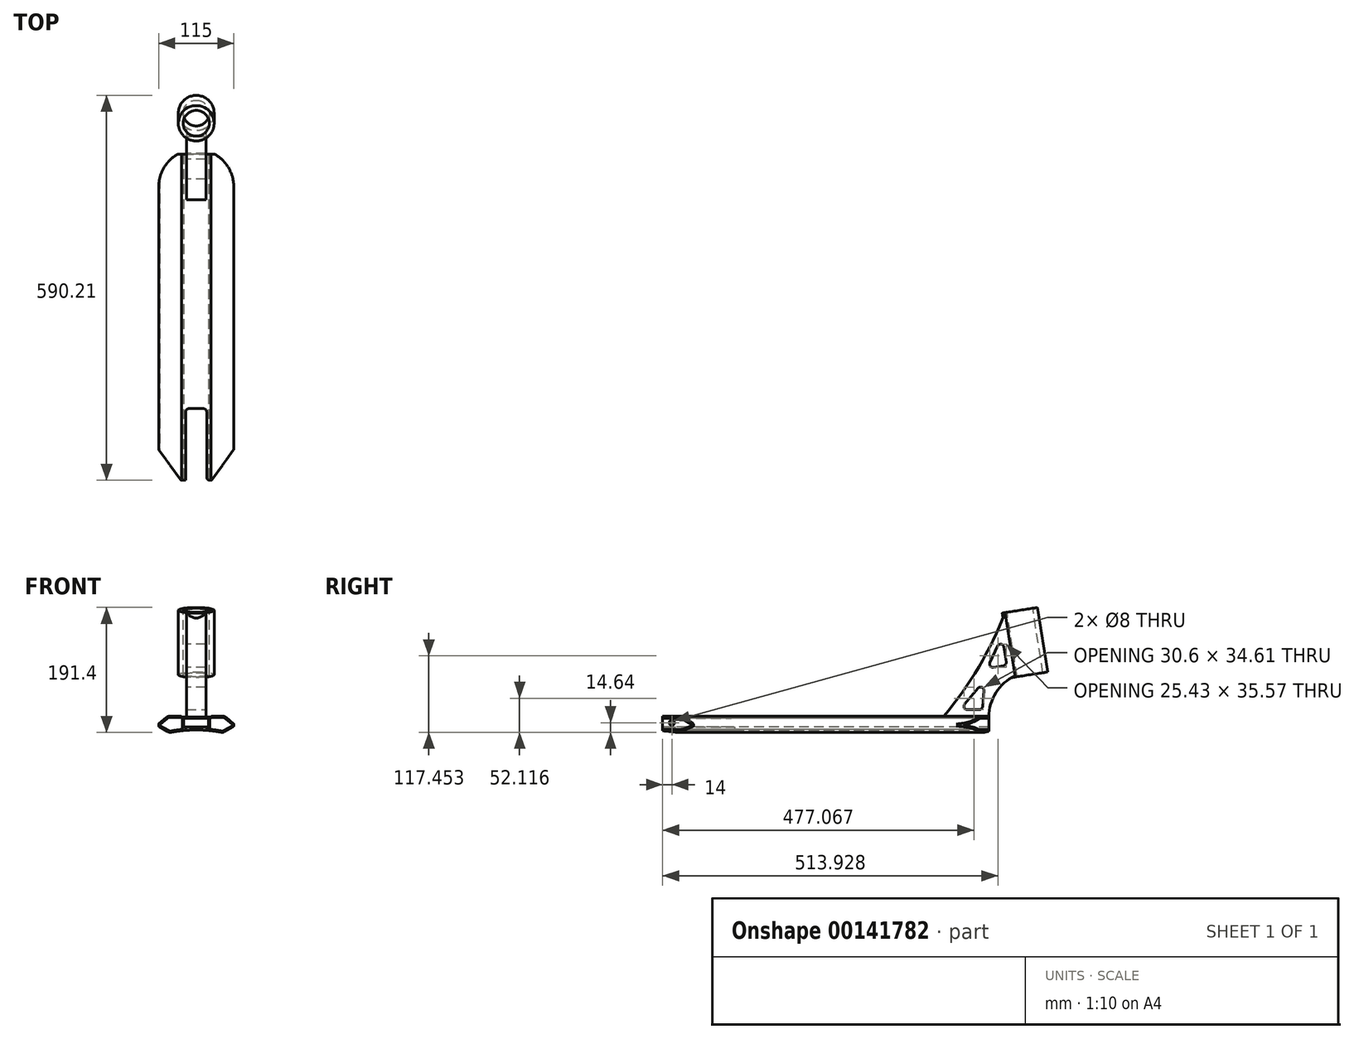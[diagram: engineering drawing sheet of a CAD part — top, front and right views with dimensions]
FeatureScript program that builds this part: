
annotation { "Feature Type Name" : "Feature", "Feature Type Description" : "" }
export const myFeature = defineFeature(function(context is Context, id is Id, definition is map)
    precondition{}
    {
        {
            var Q0;
            Q0=qCreatedBy(makeId("Front.planeOp"),FACE);
            var sketch = newSketch(context, id + "F0", { "sketchPlane" : qUnion([Q0])});
            skLineSegment(sketch, "E0", {"start": v(0, 0) * mm, "end": v(0, 43.35) * mm, "construction": true});
            skLineSegment(sketch, "E1", {"start": v(0, 25.68) * mm, "end": v(22.5, 25.68) * mm});
            skLineSegment(sketch, "E2", {"start": v(22.5, 25.68) * mm, "end": v(22.5, 26.98) * mm});
            skLineSegment(sketch, "E3", {"start": v(22.5, 26.98) * mm, "end": v(43.54, 26.98) * mm});
            skLineSegment(sketch, "E4", {"start": v(43.54, 26.98) * mm, "end": v(57.5, 15.27) * mm});
            skLineSegment(sketch, "E5", {"start": v(57.5, 15.27) * mm, "end": v(57.5, 11.27) * mm});
            skLineSegment(sketch, "E6", {"start": v(57.5, 11.27) * mm, "end": v(40.89, 1.68) * mm});
            skLineSegment(sketch, "E7.MirrorCS", {"start": v(-22.5, 26.98) * mm, "end": v(-43.54, 26.98) * mm});
            skLineSegment(sketch, "E8.MirrorCS", {"start": v(-22.5, 25.68) * mm, "end": v(-22.5, 26.98) * mm});
            skLineSegment(sketch, "E9.MirrorCS", {"start": v(-43.54, 26.98) * mm, "end": v(-57.5, 15.27) * mm});
            skLineSegment(sketch, "E10.MirrorCS", {"start": v(-57.5, 11.27) * mm, "end": v(-40.89, 1.68) * mm});
            skLineSegment(sketch, "E11.MirrorCS", {"start": v(0, 25.68) * mm, "end": v(-22.5, 25.68) * mm});
            skLineSegment(sketch, "E12.MirrorCS", {"start": v(-57.5, 15.27) * mm, "end": v(-57.5, 11.27) * mm});
            skArc(sketch, "E13", {"start": v(40.89, 1.68) * mm, "mid": v(0, 5.9) * mm, "end": v(-40.89, 1.68) * mm});
            skSolve(sketch);
        }
        {
            var Q0;
            Q0 = qSketchRegion(id + "F0", true);
            extrude(context, id + "F1", {"entities" : qUnion([Q0]), "endBound" : BoundingType.SYMMETRIC, "depth" : 500 * mm});
        }
        {
            var Q0;
            Q0=qCreatedBy(makeId("Front.planeOp"),FACE);
            var sketch = newSketch(context, id + "F2", { "sketchPlane" : qUnion([Q0])});
            skLineSegment(sketch, "E14.bottom", {"start": v(-19, 23.68) * mm, "end": v(19, 23.68) * mm});
            skLineSegment(sketch, "E14.top", {"start": v(-19, 10.68) * mm, "end": v(19, 10.68) * mm});
            skLineSegment(sketch, "E14.left", {"start": v(-19, 23.68) * mm, "end": v(-19, 10.68) * mm});
            skLineSegment(sketch, "E14.right", {"start": v(19, 23.68) * mm, "end": v(19, 10.68) * mm});
            skSolve(sketch);
        }
        {
            var Q0;
            Q0 = qSketchRegion(id + "F2", true);
            extrude(context, id + "F3", {"entities" : qUnion([Q0]), "operationType" : NewBodyOperationType.REMOVE, "endBound" : BoundingType.SYMMETRIC, "oppositeDirection" : true, "depth" : 500 * mm});
        }
        {
            var Q0;
            Q0=makeQuery(id+"F1.opExtrude","SWEPT_EDGE",EDGE,{"disambiguationData":[OSD([sQuery(id+"F0.wireOp",EDGE,"E7.MirrorCS"),sQuery(id+"F0.wireOp",EDGE,"E8.MirrorCS")])]});
            var Q1;
            Q1=makeQuery(id+"F1.opExtrude","SWEPT_EDGE",EDGE,{"disambiguationData":[OSD([sQuery(id+"F0.wireOp",EDGE,"E2"),sQuery(id+"F0.wireOp",EDGE,"E3")])]});
            fillet(context, id + "F4", {"entities" : qUnion([Q0, Q1]), "radius" : 2 * mm, "tangentPropagation" : true, "allowEdgeOverflow" : false});
        }
        {
            var Q0;
            Q0=makeQuery(id+"F1.opExtrude","SWEPT_EDGE",EDGE,{"disambiguationData":[OSD([sQuery(id+"F0.wireOp",EDGE,"E3"),sQuery(id+"F0.wireOp",EDGE,"E4")])]});
            var Q1;
            Q1=makeQuery(id+"F1.opExtrude","SWEPT_EDGE",EDGE,{"disambiguationData":[OSD([sQuery(id+"F0.wireOp",EDGE,"E7.MirrorCS"),sQuery(id+"F0.wireOp",EDGE,"E9.MirrorCS")])]});
            var Q2;
            Q2=makeQuery(id+"F1.opExtrude","SWEPT_EDGE",EDGE,{"disambiguationData":[OSD([sQuery(id+"F0.wireOp",EDGE,"E10.MirrorCS"),sQuery(id+"F0.wireOp",EDGE,"E13")])]});
            var Q3;
            Q3=makeQuery(id+"F1.opExtrude","SWEPT_EDGE",EDGE,{"disambiguationData":[OSD([sQuery(id+"F0.wireOp",EDGE,"E6"),sQuery(id+"F0.wireOp",EDGE,"E13")])]});
            fillet(context, id + "F5", {"entities" : qUnion([Q0, Q1, Q2, Q3]), "radius" : 9 * mm, "tangentPropagation" : true, "allowEdgeOverflow" : false});
        }
        {
            var Q0;
            Q0=makeQuery(id+"F1.opExtrude","SWEPT_EDGE",EDGE,{"disambiguationData":[OSD([sQuery(id+"F0.wireOp",EDGE,"E4"),sQuery(id+"F0.wireOp",EDGE,"E5")])]});
            var Q1;
            Q1=makeQuery(id+"F1.opExtrude","SWEPT_EDGE",EDGE,{"disambiguationData":[OSD([sQuery(id+"F0.wireOp",EDGE,"E5"),sQuery(id+"F0.wireOp",EDGE,"E6")])]});
            var Q2;
            Q2=makeQuery(id+"F1.opExtrude","SWEPT_EDGE",EDGE,{"disambiguationData":[OSD([sQuery(id+"F0.wireOp",EDGE,"E9.MirrorCS"),sQuery(id+"F0.wireOp",EDGE,"E12.MirrorCS")])]});
            var Q3;
            Q3=makeQuery(id+"F1.opExtrude","SWEPT_EDGE",EDGE,{"disambiguationData":[OSD([sQuery(id+"F0.wireOp",EDGE,"E10.MirrorCS"),sQuery(id+"F0.wireOp",EDGE,"E12.MirrorCS")])]});
            fillet(context, id + "F6", {"entities" : qUnion([Q0, Q1, Q2, Q3]), "radius" : 1 * mm, "tangentPropagation" : true, "allowEdgeOverflow" : false});
        }
        {
            var Q0;
            Q0=makeQuery(id+"F1.opExtrude","CAP_FACE",FACE,{"disambiguationData":[OSD([sQuery(id+"F0.wireOp",EDGE,"E1"),sQuery(id+"F0.wireOp",EDGE,"E2"),sQuery(id+"F0.wireOp",EDGE,"E3"),sQuery(id+"F0.wireOp",EDGE,"E4"),sQuery(id+"F0.wireOp",EDGE,"E5"),sQuery(id+"F0.wireOp",EDGE,"E6"),sQuery(id+"F0.wireOp",EDGE,"E7.MirrorCS"),sQuery(id+"F0.wireOp",EDGE,"E8.MirrorCS"),sQuery(id+"F0.wireOp",EDGE,"E9.MirrorCS"),sQuery(id+"F0.wireOp",EDGE,"E10.MirrorCS"),sQuery(id+"F0.wireOp",EDGE,"E11.MirrorCS"),sQuery(id+"F0.wireOp",EDGE,"E12.MirrorCS"),sQuery(id+"F0.wireOp",EDGE,"E13")])],"isStart":false});
            var sketch = newSketch(context, id + "F7", { "sketchPlane" : qUnion([Q0])});
            skLineSegment(sketch, "E15.0.0", {"start": v(-46.05, 24.87) * mm, "end": v(-57.14, 15.57) * mm});
            skArc(sketch, "E15.0.1", {"start": v(-57.14, 15.57) * mm, "mid": v(-57.4, 15.23) * mm, "end": v(-57.5, 14.8) * mm});
            skLineSegment(sketch, "E15.0.2", {"start": v(-57.5, 14.8) * mm, "end": v(-57.5, 11.85) * mm});
            skArc(sketch, "E15.0.3", {"start": v(-57.5, 11.85) * mm, "mid": v(-57.37, 11.35) * mm, "end": v(-57, 10.98) * mm});
            skLineSegment(sketch, "E15.0.4", {"start": v(-57, 10.98) * mm, "end": v(-43.83, 3.38) * mm});
            skArc(sketch, "E15.0.5", {"start": v(-43.83, 3.38) * mm, "mid": v(-40.83, 2.3) * mm, "end": v(-37.64, 2.33) * mm});
            skArc(sketch, "E15.0.6", {"start": v(-37.64, 2.33) * mm, "mid": v(0, 5.9) * mm, "end": v(37.64, 2.33) * mm});
            skArc(sketch, "E15.0.7", {"start": v(37.64, 2.33) * mm, "mid": v(40.83, 2.3) * mm, "end": v(43.83, 3.38) * mm});
            skLineSegment(sketch, "E15.0.8", {"start": v(43.83, 3.38) * mm, "end": v(57, 10.98) * mm});
            skArc(sketch, "E15.0.9", {"start": v(57, 10.98) * mm, "mid": v(57.37, 11.35) * mm, "end": v(57.5, 11.85) * mm});
            skLineSegment(sketch, "E15.0.10", {"start": v(57.5, 11.85) * mm, "end": v(57.5, 14.8) * mm});
            skArc(sketch, "E15.0.11", {"start": v(57.5, 14.8) * mm, "mid": v(57.4, 15.23) * mm, "end": v(57.14, 15.57) * mm});
            skLineSegment(sketch, "E15.0.12", {"start": v(57.14, 15.57) * mm, "end": v(46.05, 24.87) * mm});
            skArc(sketch, "E15.0.13", {"start": v(46.05, 24.87) * mm, "mid": v(43.35, 26.44) * mm, "end": v(40.27, 26.98) * mm});
            skLineSegment(sketch, "E15.0.14", {"start": v(40.27, 26.98) * mm, "end": v(24.37, 26.98) * mm});
            skArc(sketch, "E15.0.15", {"start": v(24.37, 26.98) * mm, "mid": v(23.23, 26.62) * mm, "end": v(22.5, 25.68) * mm});
            skLineSegment(sketch, "E15.0.16", {"start": v(22.5, 25.68) * mm, "end": v(-22.5, 25.68) * mm});
            skArc(sketch, "E15.0.17", {"start": v(-22.5, 25.68) * mm, "mid": v(-23.23, 26.62) * mm, "end": v(-24.37, 26.98) * mm});
            skLineSegment(sketch, "E15.0.18", {"start": v(-24.37, 26.98) * mm, "end": v(-40.27, 26.98) * mm});
            skArc(sketch, "E15.0.19", {"start": v(-40.27, 26.98) * mm, "mid": v(-43.35, 26.44) * mm, "end": v(-46.05, 24.87) * mm});
            skLineSegment(sketch, "E16.0", {"start": v(40.27, 24.98) * mm, "end": v(24.37, 24.98) * mm});
            skLineSegment(sketch, "E16.1", {"start": v(-55.61, 12.5) * mm, "end": v(-42.83, 5.1) * mm});
            skLineSegment(sketch, "E16.2", {"start": v(-44.77, 23.34) * mm, "end": v(-55.76, 14.12) * mm});
            skArc(sketch, "E16.3", {"start": v(-40.27, 24.98) * mm, "mid": v(-42.66, 24.56) * mm, "end": v(-44.77, 23.34) * mm});
            skLineSegment(sketch, "E16.4", {"start": v(-24.37, 24.98) * mm, "end": v(-40.27, 24.98) * mm});
            skArc(sketch, "E16.5", {"start": v(-42.83, 5.1) * mm, "mid": v(-40.5, 4.27) * mm, "end": v(-38.01, 4.3) * mm});
            skArc(sketch, "E16.6", {"start": v(-38.01, 4.3) * mm, "mid": v(-29.53, 5.73) * mm, "end": v(-21, 6.81) * mm});
            skArc(sketch, "E16.7", {"start": v(38.01, 4.3) * mm, "mid": v(40.5, 4.27) * mm, "end": v(42.83, 5.1) * mm});
            skLineSegment(sketch, "E16.8", {"start": v(42.83, 5.1) * mm, "end": v(55.61, 12.5) * mm});
            skLineSegment(sketch, "E16.9", {"start": v(55.76, 14.12) * mm, "end": v(44.77, 23.34) * mm});
            skArc(sketch, "E16.10", {"start": v(44.77, 23.34) * mm, "mid": v(42.66, 24.56) * mm, "end": v(40.27, 24.98) * mm});
            skLineSegment(sketch, "E17", {"start": v(-21, 23.68) * mm, "end": v(-21, 6.81) * mm});
            skLineSegment(sketch, "E18", {"start": v(-22.5, 23.68) * mm, "end": v(-21, 23.68) * mm});
            skArc(sketch, "E19", {"start": v(-22.5, 23.68) * mm, "mid": v(-23.23, 24.62) * mm, "end": v(-24.37, 24.98) * mm});
            skLineSegment(sketch, "E20", {"start": v(21, 23.68) * mm, "end": v(21, 6.81) * mm});
            skLineSegment(sketch, "E21", {"start": v(21, 23.68) * mm, "end": v(22.5, 23.68) * mm});
            skArc(sketch, "E22", {"start": v(24.37, 24.98) * mm, "mid": v(23.23, 24.62) * mm, "end": v(22.5, 23.68) * mm});
            skArc(sketch, "E23.trimOffspring", {"start": v(21, 6.81) * mm, "mid": v(29.53, 5.73) * mm, "end": v(38.01, 4.3) * mm});
            skPoint(sketch, "E24.visualSharp", {"position": v(-56.85, 13.2) * mm});
            skArc(sketch, "E24.filletArc", {"start": v(-55.76, 14.12) * mm, "mid": v(-56.1, 13.27) * mm, "end": v(-55.61, 12.5) * mm});
            skPoint(sketch, "E25.visualSharp", {"position": v(56.85, 13.2) * mm});
            skArc(sketch, "E25.filletArc", {"start": v(55.61, 12.5) * mm, "mid": v(56.1, 13.27) * mm, "end": v(55.76, 14.12) * mm});
            skSolve(sketch);
        }
        {
            var Q0;
            Q0=makeQuery(id+"F7.imprint","IMPRINT",FACE,{"disambiguationData":[TD([[makeQuery(id+"F7.imprint","IMPRINT",EDGE,{"derivedFrom":sQuery(id+"F7.wireOp",EDGE,"E16.1")}),1.0]])]});
            var Q1;
            Q1=makeQuery(id+"F7.imprint","IMPRINT",FACE,{"disambiguationData":[TD([[makeQuery(id+"F7.imprint","IMPRINT",EDGE,{"derivedFrom":sQuery(id+"F7.wireOp",EDGE,"E16.0")}),1.0]])]});
            extrude(context, id + "F8", {"entities" : qUnion([Q0, Q1]), "operationType" : NewBodyOperationType.REMOVE, "endBound" : BoundingType.THROUGH_ALL, "oppositeDirection" : true, "depth" : 25 * mm});
        }
        {
            var Q0;
            Q0=qCreatedBy(makeId("Top.planeOp"),FACE);
            var sketch = newSketch(context, id + "F9", { "sketchPlane" : qUnion([Q0])});
            skArc(sketch, "E26", {"start": v(57.5, 200) * mm, "mid": v(0, 257.5) * mm, "end": v(-57.5, 200) * mm});
            skLineSegment(sketch, "E27", {"start": v(-57.5, 200) * mm, "end": v(-57.5, 280) * mm});
            skLineSegment(sketch, "E28", {"start": v(57.5, 200) * mm, "end": v(57.5, 280) * mm});
            skLineSegment(sketch, "E29", {"start": v(57.5, 280) * mm, "end": v(-57.5, 280) * mm});
            skSolve(sketch);
        }
        {
            var Q0;
            Q0 = qSketchRegion(id + "F9", true);
            extrude(context, id + "F10", {"entities" : qUnion([Q0]), "operationType" : NewBodyOperationType.REMOVE, "endBound" : BoundingType.THROUGH_ALL, "depth" : 25 * mm});
        }
        {
            var Q0;
            Q0=qCreatedBy(makeId("Top.planeOp"),FACE);
            var sketch = newSketch(context, id + "F11", { "sketchPlane" : qUnion([Q0])});
            skLineSegment(sketch, "E30", {"start": v(-57.5, -203) * mm, "end": v(-57.5, -303) * mm});
            skLineSegment(sketch, "E31", {"start": v(-57.5, -303) * mm, "end": v(57.5, -303) * mm});
            skLineSegment(sketch, "E32", {"start": v(57.5, -303) * mm, "end": v(57.5, -203) * mm});
            skLineSegment(sketch, "E33", {"start": v(57.5, -203) * mm, "end": v(23.35, -250) * mm});
            skLineSegment(sketch, "E34", {"start": v(23.35, -250) * mm, "end": v(16, -250) * mm});
            skLineSegment(sketch, "E35", {"start": v(16, -250) * mm, "end": v(16, -140) * mm});
            skLineSegment(sketch, "E36", {"start": v(16, -140) * mm, "end": v(-16, -140) * mm});
            skLineSegment(sketch, "E37", {"start": v(-16, -140) * mm, "end": v(-16, -250) * mm});
            skLineSegment(sketch, "E38", {"start": v(-16, -250) * mm, "end": v(-23.35, -250) * mm});
            skLineSegment(sketch, "E39", {"start": v(-23.35, -250) * mm, "end": v(-57.5, -203) * mm});
            skLineSegment(sketch, "E40.bottom", {"start": v(57.5, -203) * mm, "end": v(68, -203) * mm});
            skLineSegment(sketch, "E40.top", {"start": v(57.5, -257) * mm, "end": v(68, -257) * mm});
            skLineSegment(sketch, "E40.left", {"start": v(57.5, -203) * mm, "end": v(57.5, -257) * mm});
            skLineSegment(sketch, "E40.right", {"start": v(68, -203) * mm, "end": v(68, -257) * mm});
            skLineSegment(sketch, "E41.bottom", {"start": v(-57.5, -203) * mm, "end": v(-68, -203) * mm});
            skLineSegment(sketch, "E41.top", {"start": v(-57.5, -257) * mm, "end": v(-68, -257) * mm});
            skLineSegment(sketch, "E41.left", {"start": v(-57.5, -203) * mm, "end": v(-57.5, -257) * mm});
            skLineSegment(sketch, "E41.right", {"start": v(-68, -203) * mm, "end": v(-68, -257) * mm});
            skSolve(sketch);
        }
        {
            var Q0;
            Q0 = qSketchRegion(id + "F11", true);
            extrude(context, id + "F12", {"entities" : qUnion([Q0]), "operationType" : NewBodyOperationType.REMOVE, "endBound" : BoundingType.THROUGH_ALL, "depth" : 25 * mm});
        }
        {
            var Q0;
            {var subQ2=sQuery(id+"F11.wireOp",EDGE,"E37");Q0=makeQuery(id+"F12.boolean.opBoolean","COPY",EDGE,{"disambiguationData":[TD([makeQuery(id+"F3.boolean.opBoolean","COPY",FACE,{"derivedFrom":makeQuery(id+"F3.opExtrude","SWEPT_FACE",FACE,{"disambiguationData":[OSD([sQuery(id+"F2.wireOp",EDGE,"E14.bottom")])]})})])],"derivedFrom":makeQuery(id+"F12.opExtrude","SWEPT_EDGE",EDGE,{"disambiguationData":[OSD([subQ2,sQuery(id+"F11.wireOp",EDGE,"E38")])]})});}
            var Q1;
            {var subQ0=sQuery(id+"F11.wireOp",EDGE,"E36");var subQ1=sQuery(id+"F11.wireOp",EDGE,"E37");Q1=makeQuery(id+"F12.boolean.opBoolean","COPY",EDGE,{"disambiguationData":[TD([makeQuery(id+"F3.boolean.opBoolean","COPY",FACE,{"derivedFrom":makeQuery(id+"F3.opExtrude","SWEPT_FACE",FACE,{"disambiguationData":[OSD([sQuery(id+"F2.wireOp",EDGE,"E14.bottom")])]})})])],"derivedFrom":makeQuery(id+"F12.opExtrude","SWEPT_EDGE",EDGE,{"disambiguationData":[OSD([subQ0,subQ1])]})});}
            var Q2;
            {var subQ0=sQuery(id+"F11.wireOp",EDGE,"E36");var subQ1=sQuery(id+"F11.wireOp",EDGE,"E37");Q2=makeQuery(id+"F12.boolean.opBoolean","COPY",EDGE,{"disambiguationData":[TD([makeQuery(id+"F1.opExtrude","SWEPT_FACE",FACE,{"disambiguationData":[OSD([sQuery(id+"F0.wireOp",EDGE,"E13")])]})])],"derivedFrom":makeQuery(id+"F12.opExtrude","SWEPT_EDGE",EDGE,{"disambiguationData":[OSD([subQ0,subQ1])]})});}
            var Q3;
            {var subQ2=sQuery(id+"F11.wireOp",EDGE,"E35");Q3=makeQuery(id+"F12.boolean.opBoolean","COPY",EDGE,{"disambiguationData":[TD([makeQuery(id+"F3.boolean.opBoolean","COPY",FACE,{"derivedFrom":makeQuery(id+"F3.opExtrude","SWEPT_FACE",FACE,{"disambiguationData":[OSD([sQuery(id+"F2.wireOp",EDGE,"E14.bottom")])]})})])],"derivedFrom":makeQuery(id+"F12.opExtrude","SWEPT_EDGE",EDGE,{"disambiguationData":[OSD([sQuery(id+"F11.wireOp",EDGE,"E34"),subQ2])]})});}
            var Q4;
            {var subQ0=sQuery(id+"F11.wireOp",EDGE,"E35");var subQ1=sQuery(id+"F11.wireOp",EDGE,"E36");Q4=makeQuery(id+"F12.boolean.opBoolean","COPY",EDGE,{"disambiguationData":[TD([makeQuery(id+"F1.opExtrude","SWEPT_FACE",FACE,{"disambiguationData":[OSD([sQuery(id+"F0.wireOp",EDGE,"E13")])]})])],"derivedFrom":makeQuery(id+"F12.opExtrude","SWEPT_EDGE",EDGE,{"disambiguationData":[OSD([subQ0,subQ1])]})});}
            var Q5;
            {var subQ0=sQuery(id+"F11.wireOp",EDGE,"E35");var subQ1=sQuery(id+"F11.wireOp",EDGE,"E36");Q5=makeQuery(id+"F12.boolean.opBoolean","COPY",EDGE,{"disambiguationData":[TD([makeQuery(id+"F3.boolean.opBoolean","COPY",FACE,{"derivedFrom":makeQuery(id+"F3.opExtrude","SWEPT_FACE",FACE,{"disambiguationData":[OSD([sQuery(id+"F2.wireOp",EDGE,"E14.bottom")])]})})])],"derivedFrom":makeQuery(id+"F12.opExtrude","SWEPT_EDGE",EDGE,{"disambiguationData":[OSD([subQ0,subQ1])]})});}
            fillet(context, id + "F13", {"entities" : qUnion([Q0, Q1, Q2, Q3, Q4, Q5]), "radius" : 5 * mm, "tangentPropagation" : true, "allowEdgeOverflow" : false});
        }
        {
            var Q0;
            Q0=qCreatedBy(makeId("Right.planeOp"),FACE);
            var sketch = newSketch(context, id + "F14", { "sketchPlane" : qUnion([Q0])});
            skLineSegment(sketch, "E42", {"start": v(250, 25.68) * mm, "end": v(180, 25.68) * mm});
            skArc(sketch, "E43", {"start": v(180, 25.68) * mm, "mid": v(234.18, 101.65) * mm, "end": v(274.73, 185.68) * mm});
            skLineSegment(sketch, "E44", {"start": v(274.73, 185.68) * mm, "end": v(320.16, 192.88) * mm});
            skLineSegment(sketch, "E45", {"start": v(320.16, 192.88) * mm, "end": v(335.8, 94.1) * mm});
            skLineSegment(sketch, "E46", {"start": v(335.8, 94.1) * mm, "end": v(290.37, 86.91) * mm});
            skLineSegment(sketch, "E47", {"start": v(290.37, 86.91) * mm, "end": v(290.05, 88.95) * mm});
            skArc(sketch, "E48", {"start": v(290.05, 88.95) * mm, "mid": v(260.85, 63.12) * mm, "end": v(250, 25.68) * mm});
            skSolve(sketch);
        }
        {
            var Q0;
            Q0 = qSketchRegion(id + "F14", true);
            extrude(context, id + "F15", {"entities" : qUnion([Q0]), "operationType" : NewBodyOperationType.ADD, "endBound" : BoundingType.SYMMETRIC, "depth" : 30 * mm});
        }
        {
            var Q0;
            Q0=makeQuery(id+"F15.opExtrude","SWEPT_FACE",FACE,{"disambiguationData":[OSD([sQuery(id+"F14.wireOp",EDGE,"E44")])]});
            var sketch = newSketch(context, id + "F16", { "sketchPlane" : qUnion([Q0])});
            skCircle(sketch, "E49", {"center": v(0, 323.4) * mm, "radius": 27.46 * mm});
            skPoint(sketch, "E50", {"position": v(15, 346.4) * mm});
            skSolve(sketch);
        }
        {
            var Q0;
            Q0 = qSketchRegion(id + "F16", true);
            var Q1;
            Q1=makeQuery(id+"F15.opExtrude","SWEPT_FACE",FACE,{"disambiguationData":[OSD([sQuery(id+"F14.wireOp",EDGE,"E46")])]});
            extrude(context, id + "F17", {"entities" : qUnion([Q0]), "operationType" : NewBodyOperationType.ADD, "endBound" : BoundingType.UP_TO_SURFACE, "oppositeDirection" : true, "endBoundEntityFace" : qUnion([Q1]), "depth" : 25 * mm});
        }
        {
            var Q0;
            Q0=makeQuery(id+"F17.boolean.opBoolean","MERGE",FACE,{"derivedFrom":[makeQuery(id+"F15.opExtrude","SWEPT_FACE",FACE,{"disambiguationData":[OSD([sQuery(id+"F14.wireOp",EDGE,"E44")])]}),makeQuery(id+"F17.opExtrude","CAP_FACE",FACE,{"disambiguationData":[OSD([sQuery(id+"F16.wireOp",EDGE,"E49")])],"isStart":true})]});
            var sketch = newSketch(context, id + "F18", { "sketchPlane" : qUnion([Q0])});
            skPoint(sketch, "E51", {"position": v(0, 323.4) * mm});
            skSolve(sketch);
        }
        {
            var Q0;
            Q0=sQuery(id+"F18.wireOp",VERTEX,"E51");
            var Q1;
            Q1=makeQuery(id+"F1.opExtrude","SWEPT_BODY",BODY,{"disambiguationData":[OSD([sQuery(id+"F0.wireOp",EDGE,"E1"),sQuery(id+"F0.wireOp",EDGE,"E2"),sQuery(id+"F0.wireOp",EDGE,"E3"),sQuery(id+"F0.wireOp",EDGE,"E4"),sQuery(id+"F0.wireOp",EDGE,"E5"),sQuery(id+"F0.wireOp",EDGE,"E6"),sQuery(id+"F0.wireOp",EDGE,"E7.MirrorCS"),sQuery(id+"F0.wireOp",EDGE,"E8.MirrorCS"),sQuery(id+"F0.wireOp",EDGE,"E9.MirrorCS"),sQuery(id+"F0.wireOp",EDGE,"E10.MirrorCS"),sQuery(id+"F0.wireOp",EDGE,"E11.MirrorCS"),sQuery(id+"F0.wireOp",EDGE,"E12.MirrorCS"),sQuery(id+"F0.wireOp",EDGE,"E13")])]});
            hole(context, id + "F19", {"style" : HoleStyle.SIMPLE, "endStyle" : HoleEndStyle.THROUGH, "holeDiameter" : 40 * mm, "locations" : qUnion([Q0]), "scope" : qUnion([Q1]), "isTappedThrough" : true});
        }
        {
            var Q0;
            Q0=makeQuery(id+"F8.boolean.opBoolean","COPY",FACE,{"derivedFrom":makeQuery(id+"F8.opExtrude","SWEPT_FACE",FACE,{"disambiguationData":[OSD([sQuery(id+"F7.wireOp",EDGE,"E20")])]})});
            var sketch = newSketch(context, id + "F20", { "sketchPlane" : qUnion([Q0])});
            skPoint(sketch, "E52", {"position": v(-236, 16.81) * mm});
            skSolve(sketch);
        }
        {
            var Q0;
            Q0=sQuery(id+"F20.wireOp",VERTEX,"E52");
            var Q1;
            Q1=makeQuery(id+"F1.opExtrude","SWEPT_BODY",BODY,{"disambiguationData":[OSD([sQuery(id+"F0.wireOp",EDGE,"E1"),sQuery(id+"F0.wireOp",EDGE,"E2"),sQuery(id+"F0.wireOp",EDGE,"E3"),sQuery(id+"F0.wireOp",EDGE,"E4"),sQuery(id+"F0.wireOp",EDGE,"E5"),sQuery(id+"F0.wireOp",EDGE,"E6"),sQuery(id+"F0.wireOp",EDGE,"E7.MirrorCS"),sQuery(id+"F0.wireOp",EDGE,"E8.MirrorCS"),sQuery(id+"F0.wireOp",EDGE,"E9.MirrorCS"),sQuery(id+"F0.wireOp",EDGE,"E10.MirrorCS"),sQuery(id+"F0.wireOp",EDGE,"E11.MirrorCS"),sQuery(id+"F0.wireOp",EDGE,"E12.MirrorCS"),sQuery(id+"F0.wireOp",EDGE,"E13")])]});
            hole(context, id + "F21", {"style" : HoleStyle.SIMPLE, "endStyle" : HoleEndStyle.THROUGH, "holeDiameter" : 8 * mm, "locations" : qUnion([Q0]), "scope" : qUnion([Q1]), "isTappedThrough" : true});
        }
        {
            var Q0;
            Q0=makeQuery(id+"F15.opExtrude","CAP_FACE",FACE,{"disambiguationData":[OSD([sQuery(id+"F14.wireOp",EDGE,"E42"),sQuery(id+"F14.wireOp",EDGE,"E43"),sQuery(id+"F14.wireOp",EDGE,"E44"),sQuery(id+"F14.wireOp",EDGE,"E45"),sQuery(id+"F14.wireOp",EDGE,"E46"),sQuery(id+"F14.wireOp",EDGE,"E47"),sQuery(id+"F14.wireOp",EDGE,"E48")])],"isStart":false});
            var sketch = newSketch(context, id + "F22", { "sketchPlane" : qUnion([Q0])});
            skLineSegment(sketch, "E53", {"start": v(206, 36.98) * mm, "end": v(240, 36.98) * mm});
            skLineSegment(sketch, "E54", {"start": v(240, 36.98) * mm, "end": v(243.64, 81.83) * mm});
            skLineSegment(sketch, "E55", {"start": v(243.64, 81.83) * mm, "end": v(206, 36.98) * mm});
            skLineSegment(sketch, "E56", {"start": v(270.33, 149.55) * mm, "end": v(277.37, 105.1) * mm});
            skLineSegment(sketch, "E57", {"start": v(277.37, 105.1) * mm, "end": v(247.74, 100.4) * mm});
            skLineSegment(sketch, "E58", {"start": v(247.74, 100.4) * mm, "end": v(270.33, 149.55) * mm});
            skSolve(sketch);
        }
        {
            var Q0;
            Q0 = qSketchRegion(id + "F22", true);
            extrude(context, id + "F23", {"entities" : qUnion([Q0]), "operationType" : NewBodyOperationType.REMOVE, "endBound" : BoundingType.THROUGH_ALL, "oppositeDirection" : true, "depth" : 25 * mm});
        }
        {
            var Q0;
            Q0=makeQuery(id+"F23.boolean.opBoolean","COPY",EDGE,{"derivedFrom":makeQuery(id+"F23.opExtrude","SWEPT_EDGE",EDGE,{"disambiguationData":[OSD([sQuery(id+"F22.wireOp",EDGE,"E56"),sQuery(id+"F22.wireOp",EDGE,"E58")])]})});
            var Q1;
            Q1=makeQuery(id+"F23.boolean.opBoolean","COPY",EDGE,{"derivedFrom":makeQuery(id+"F23.opExtrude","SWEPT_EDGE",EDGE,{"disambiguationData":[OSD([sQuery(id+"F22.wireOp",EDGE,"E53"),sQuery(id+"F22.wireOp",EDGE,"E54")])]})});
            var Q2;
            Q2=makeQuery(id+"F23.boolean.opBoolean","COPY",EDGE,{"derivedFrom":makeQuery(id+"F23.opExtrude","SWEPT_EDGE",EDGE,{"disambiguationData":[OSD([sQuery(id+"F22.wireOp",EDGE,"E56"),sQuery(id+"F22.wireOp",EDGE,"E57")])]})});
            var Q3;
            Q3=makeQuery(id+"F23.boolean.opBoolean","COPY",EDGE,{"derivedFrom":makeQuery(id+"F23.opExtrude","SWEPT_EDGE",EDGE,{"disambiguationData":[OSD([sQuery(id+"F22.wireOp",EDGE,"E54"),sQuery(id+"F22.wireOp",EDGE,"E55")])]})});
            var Q4;
            Q4=makeQuery(id+"F23.boolean.opBoolean","COPY",EDGE,{"derivedFrom":makeQuery(id+"F23.opExtrude","SWEPT_EDGE",EDGE,{"disambiguationData":[OSD([sQuery(id+"F22.wireOp",EDGE,"E57"),sQuery(id+"F22.wireOp",EDGE,"E58")])]})});
            var Q5;
            Q5=makeQuery(id+"F23.boolean.opBoolean","COPY",EDGE,{"derivedFrom":makeQuery(id+"F23.opExtrude","SWEPT_EDGE",EDGE,{"disambiguationData":[OSD([sQuery(id+"F22.wireOp",EDGE,"E53"),sQuery(id+"F22.wireOp",EDGE,"E55")])]})});
            fillet(context, id + "F24", {"entities" : qUnion([Q0, Q1, Q2, Q3, Q4, Q5]), "radius" : 5 * mm, "tangentPropagation" : true, "allowEdgeOverflow" : false});
        }
    });
